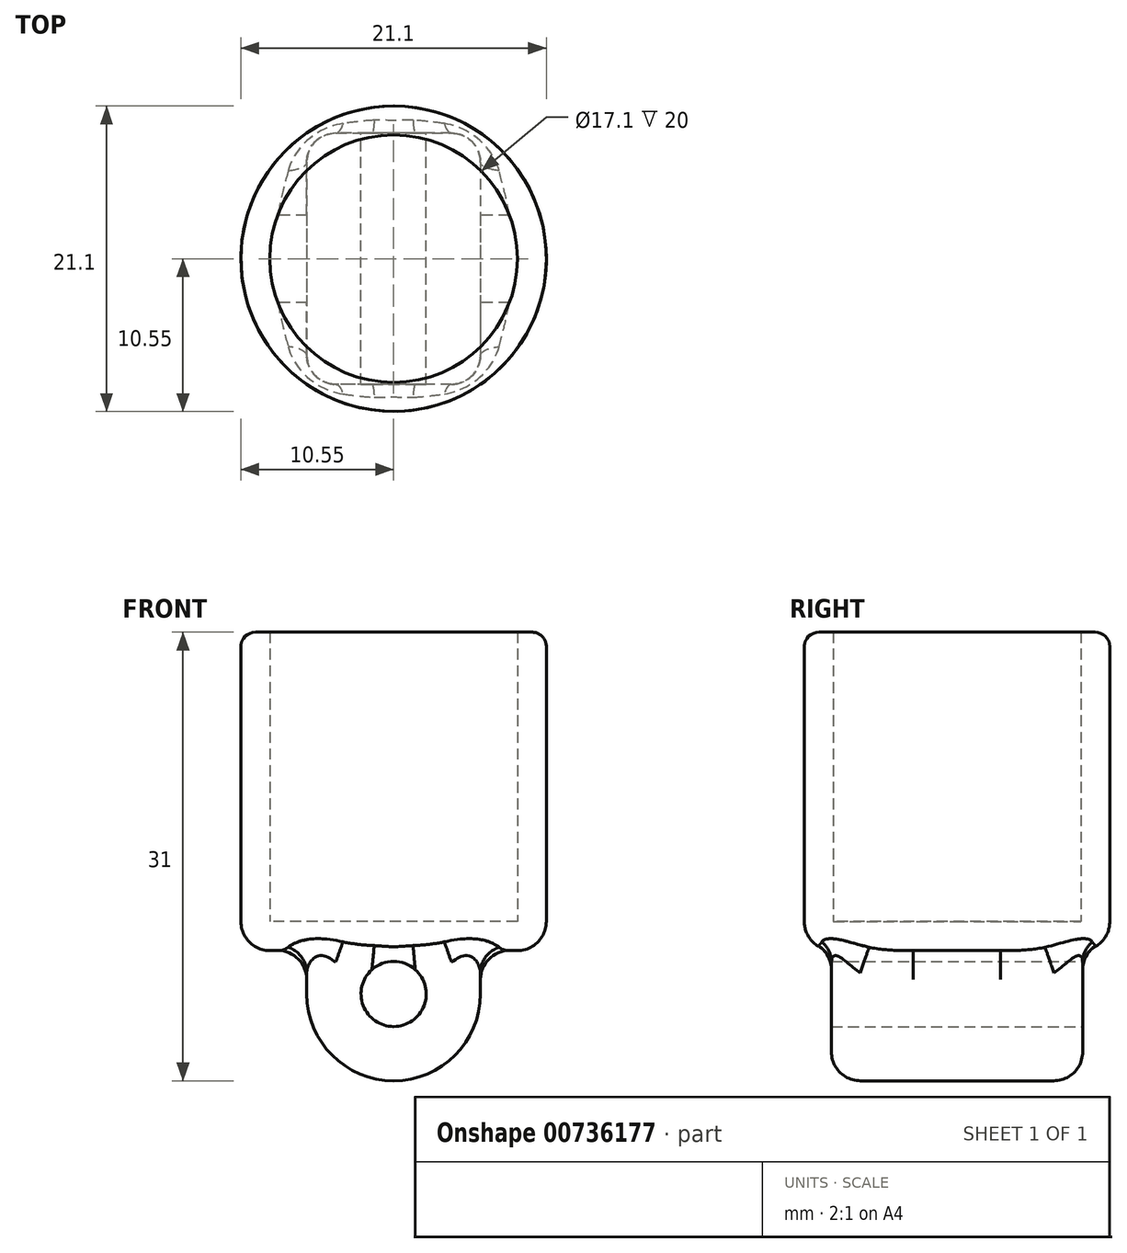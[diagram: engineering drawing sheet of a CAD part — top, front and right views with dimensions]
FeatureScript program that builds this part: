
annotation { "Feature Type Name" : "Feature", "Feature Type Description" : "" }
export const myFeature = defineFeature(function(context is Context, id is Id, definition is map)
    precondition{}
    {
        {
            var Q0;
            Q0=qCreatedBy(makeId("Top.planeOp"),FACE);
            var sketch = newSketch(context, id + "F0", { "sketchPlane" : qUnion([Q0])});
            skCircle(sketch, "E0", {"center": v(0, 0) * mm, "radius": 8.55 * mm});
            skCircle(sketch, "E1", {"center": v(0, 0) * mm, "radius": 10.55 * mm});
            skSolve(sketch);
        }
        {
            var Q0;
            Q0=makeQuery(id+"F0.imprint","IMPRINT",FACE,{"disambiguationData":[TD([[makeQuery(id+"F0.imprint","IMPRINT",EDGE,{"derivedFrom":sQuery(id+"F0.wireOp",EDGE,"E0")}),-1.0]])]});
            extrude(context, id + "F1", {"entities" : qUnion([Q0]), "depth" : 20 * mm, "offsetDistance" : 25 * mm});
        }
        {
            var Q0;
            Q0=makeQuery(id+"F0.imprint","IMPRINT",FACE,{"disambiguationData":[TD([[makeQuery(id+"F0.imprint","IMPRINT",EDGE,{"derivedFrom":sQuery(id+"F0.wireOp",EDGE,"E0")}),1.0]])]});
            var Q1;
            Q1=makeQuery(id+"F0.imprint","IMPRINT",FACE,{"disambiguationData":[TD([[makeQuery(id+"F0.imprint","IMPRINT",EDGE,{"derivedFrom":sQuery(id+"F0.wireOp",EDGE,"E0")}),-1.0]])]});
            extrude(context, id + "F2", {"entities" : qUnion([Q0, Q1]), "operationType" : NewBodyOperationType.ADD, "oppositeDirection" : true, "depth" : 2 * mm, "offsetDistance" : 25 * mm});
        }
        {
            var Q0;
            Q0=makeQuery(id+"F2.opExtrude","CAP_FACE",FACE,{"disambiguationData":[OSD([sQuery(id+"F0.wireOp",EDGE,"E1")])],"isStart":false});
            var sketch = newSketch(context, id + "F3", { "sketchPlane" : qUnion([Q0])});
            skLineSegment(sketch, "E2.bottom", {"start": v(6, -8.68) * mm, "end": v(-6, -8.68) * mm});
            skLineSegment(sketch, "E2.top", {"start": v(6, 8.68) * mm, "end": v(-6, 8.68) * mm});
            skLineSegment(sketch, "E2.left", {"start": v(6, -8.68) * mm, "end": v(6, 8.68) * mm});
            skLineSegment(sketch, "E2.right", {"start": v(-6, -8.68) * mm, "end": v(-6, 8.68) * mm});
            skPoint(sketch, "E2.middle", {"position": v(0, 0) * mm});
            skSolve(sketch);
        }
        {
            var Q0;
            Q0=makeQuery(id+"F2.opExtrude","CAP_EDGE",EDGE,{"disambiguationData":[OSD([sQuery(id+"F0.wireOp",EDGE,"E1")])],"isStart":false});
            fillet(context, id + "F4", {"entities" : qUnion([Q0]), "radius" : 2 * mm, "tangentPropagation" : true, "allowEdgeOverflow" : false});
        }
        {
            var Q0;
            Q0=makeQuery(id+"F3.imprint","IMPRINT",FACE,{"disambiguationData":[TD([[makeQuery(id+"F3.imprint","IMPRINT",EDGE,{"derivedFrom":sQuery(id+"F3.wireOp",EDGE,"E2.bottom")}),-1.0]])]});
            extrude(context, id + "F5", {"entities" : qUnion([Q0]), "operationType" : NewBodyOperationType.ADD, "depth" : 9 * mm, "offsetDistance" : 25 * mm, "hasSecondDirection" : true, "secondDirectionOppositeDirection" : true, "secondDirectionDepth" : 2 * mm});
        }
        {
            var Q0;
            Q0=makeQuery(id+"F5.opExtrude","CAP_EDGE",EDGE,{"disambiguationData":[OSD([sQuery(id+"F3.wireOp",EDGE,"E2.right")])],"isStart":false});
            var Q1;
            Q1=makeQuery(id+"F5.opExtrude","CAP_EDGE",EDGE,{"disambiguationData":[OSD([sQuery(id+"F3.wireOp",EDGE,"E2.left")])],"isStart":false});
            fillet(context, id + "F6", {"entities" : qUnion([Q0, Q1]), "radius" : 6 * mm, "tangentPropagation" : true, "allowEdgeOverflow" : false});
        }
        {
            var Q0;
            Q0=makeQuery(id+"F5.opExtrude","SWEPT_FACE",FACE,{"disambiguationData":[OSD([sQuery(id+"F3.wireOp",EDGE,"E2.bottom")])]});
            var sketch = newSketch(context, id + "F7", { "sketchPlane" : qUnion([Q0])});
            skCircle(sketch, "E3", {"center": v(0, -5) * mm, "radius": 2.25 * mm});
            skSolve(sketch);
        }
        {
            var Q0;
            Q0=makeQuery(id+"F7.imprint","IMPRINT",FACE,{"disambiguationData":[TD([[makeQuery(id+"F7.imprint","IMPRINT",EDGE,{"derivedFrom":sQuery(id+"F7.wireOp",EDGE,"E3")}),1.0]])]});
            extrude(context, id + "F8", {"entities" : qUnion([Q0]), "operationType" : NewBodyOperationType.REMOVE, "oppositeDirection" : true, "depth" : 25 * mm, "offsetDistance" : 25 * mm});
        }
        {
            var Q0;
            Q0=makeQuery(id+"F6.opFillet","BLEND_EDGE",EDGE,{"blendedFrom":[makeQuery(id+"F5.opExtrude","CAP_EDGE",EDGE,{"disambiguationData":[OSD([sQuery(id+"F3.wireOp",EDGE,"E2.left")])],"isStart":false}),makeQuery(id+"F5.opExtrude","SWEPT_FACE",FACE,{"disambiguationData":[OSD([sQuery(id+"F3.wireOp",EDGE,"E2.top")])]})],"blendedInto":[makeQuery(id+"F5.opExtrude","SWEPT_FACE",FACE,{"disambiguationData":[OSD([sQuery(id+"F3.wireOp",EDGE,"E2.top")])]})]});
            var Q1;
            Q1=makeQuery(id+"F6.opFillet","BLEND_EDGE",EDGE,{"blendedFrom":[makeQuery(id+"F5.opExtrude","CAP_EDGE",EDGE,{"disambiguationData":[OSD([sQuery(id+"F3.wireOp",EDGE,"E2.left")])],"isStart":false}),makeQuery(id+"F5.opExtrude","SWEPT_FACE",FACE,{"disambiguationData":[OSD([sQuery(id+"F3.wireOp",EDGE,"E2.bottom")])]})],"blendedInto":[makeQuery(id+"F5.opExtrude","SWEPT_FACE",FACE,{"disambiguationData":[OSD([sQuery(id+"F3.wireOp",EDGE,"E2.bottom")])]})]});
            fillet(context, id + "F9", {"entities" : qUnion([Q0, Q1]), "radius" : 2 * mm, "tangentPropagation" : true, "allowEdgeOverflow" : false});
        }
        {
            var Q0;
            Q0=makeQuery(id+"F5.boolean.opBoolean","INTERSECT",EDGE,{"derivedFrom":[makeQuery(id+"F2.opExtrude","CAP_FACE",FACE,{"disambiguationData":[OSD([sQuery(id+"F0.wireOp",EDGE,"E1")])],"isStart":false}),makeQuery(id+"F5.opExtrude","SWEPT_FACE",FACE,{"disambiguationData":[OSD([sQuery(id+"F3.wireOp",EDGE,"E2.right")])]})]});
            fillet(context, id + "F10", {"entities" : qUnion([Q0]), "radius" : 2 * mm, "tangentPropagation" : true, "allowEdgeOverflow" : false});
        }
        {
            var Q0;
            Q0=makeQuery(id+"F1.opExtrude","CAP_EDGE",EDGE,{"disambiguationData":[OSD([sQuery(id+"F0.wireOp",EDGE,"E1")])],"isStart":false});
            fillet(context, id + "F11", {"entities" : qUnion([Q0]), "radius" : 1 * mm, "tangentPropagation" : true, "allowEdgeOverflow" : false});
        }
    });
